FCSTD DOCUMENT  (FreeCAD 1.0R38642 (Git))
Label: heatsink2
License: All rights reserved
LicenseURL: https://en.wikipedia.org/wiki/All_rights_reserved
objects: Sketcher::SketchObject×9, Part::Cut×6, PartDesign::SubShapeBinder×5, Part::Mirroring×5, PartDesign::Fillet×4, PartDesign::Body×4, PartDesign::Pad×3, PartDesign::Plane×3, Fem::FeaturePython×3, PartDesign::AdditivePipe×2, Spreadsheet::Sheet×1, PartDesign::LinearPattern×1, Part::FeaturePython×1, Fem::FemMeshShapeBaseObjectPython×1
note: 71 computed .brp shape members not serialized (recipe doc carries the construction recipe); baked Part::Feature solids carry a one-line shape summary decoded from their .brp

FEATURE [Spreadsheet::Sheet] Spreadsheet
  cells = A1='Base Plate; A2='size; B2(base_size)==50 mm; A3='thickness; B3(base_thickness)==4 mm; A4='radius; B4(base_radius)==3 mm; A5='fillet; B5(base_fillet)==1 mm; A7='Pipes; A8='diameter; B8(pipe_diam)==7 mm; A9='distance; B9(pipe_distance)==(base_size - 3 * pipe_diam) / 4; A10='lower height; B10(pipe_lheight)==30 mm; A11='upper distance; B11(pipe_udistance)==(body_size - 3 * pipe_diam) / 4; A12='lower straight; B12(pipe_lstraight)==5 mm; A13='spline param; B13(pipe_splinep)==20 mm; A14='upper height; B14(pipe_uheight)==5 mm; A15='fillet; B15(pipe_fillet)==2.5 mm; A17='Main body; A18='size; B18(body_size)==100 mm; A19='height; B19(body_height)==75 mm; A21='Fins; A22='fillet; B22(fin_fillet)==2 mm; A23='middle space; B23(fin_mspace)==15 mm; A24='dent; B24(fin_dent)==6 mm; A25='thickness; B25(fin_thickness)==1 mm; A26='count; B26(fin_count)=20
FEATURE [Sketcher::SketchObject] Sketch
  ArcFitTolerance = 1e-06
  AttachmentSupport = -> [XY_Plane]
  FullyConstrained = true
  MakeInternals = false
  MapMode = 5
  expr: Constraints[8] = Spreadsheet.base_size
  sketch-geometry (4):
    g0: LineSegment StartX=-25 StartY=25 StartZ=0 EndX=-25 EndY=-25 EndZ=0
    g1: LineSegment StartX=-25 StartY=-25 StartZ=0 EndX=25 EndY=-25 EndZ=0
    g2: LineSegment StartX=25 StartY=-25 StartZ=0 EndX=25 EndY=25 EndZ=0
    g3: LineSegment StartX=25 StartY=25 StartZ=0 EndX=-25 EndY=25 EndZ=0
  constraints (11):
    c: Coincident(g0,g1)
    c: Coincident(g1,g2)
    c: Coincident(g2,g3)
    c: Coincident(g3,g0)
    c: Vertical(g0)
    c: Vertical(g2)
    c: Horizontal(g1)
    c: Horizontal(g3)
    c: DistanceY(g0,g0) = 50
    c: Equal(g0,g3)
    c: Symmetric(g0,g1,g-1)
FEATURE [PartDesign::Pad] Pad
  Direction = (0,0,1)
  Length = 4
  Length2 = 10
  Profile = -> Sketch
  ReferenceAxis = -> Sketch [N_Axis]
  Refine = true
  Reversed = true
  Suppressed = false
  Type = 0
  expr: Length = Spreadsheet.base_thickness
FEATURE [PartDesign::Fillet] Fillet
  Base = -> Pad [Edge5,Edge8,Edge1,Edge2]
  BaseFeature = -> Pad
  Radius = 3
  Refine = true
  SupportTransform = false
  Suppressed = false
  UseAllEdges = false
  expr: Radius = Spreadsheet.base_radius
FEATURE [Sketcher::SketchObject] Sketch001  label="PipeCenters"
  ArcFitTolerance = 1e-06
  AttachmentSupport = -> [XY_Plane001]
  FullyConstrained = true
  MakeInternals = false
  MapMode = 5
  expr: Constraints[11] = Spreadsheet.pipe_distance + Spreadsheet.pipe_diam / 2
  expr: Constraints[12] = Spreadsheet.pipe_distance + Spreadsheet.pipe_diam / 2
  expr: Constraints[14] = Spreadsheet.pipe_distance + Spreadsheet.pipe_diam
  expr: Constraints[16] = Spreadsheet.pipe_distance + Spreadsheet.pipe_diam
  expr: Constraints[9] = Spreadsheet.base_size
  sketch-geometry (7):
    g0: LineSegment [constr] StartX=-25 StartY=25 StartZ=0 EndX=-25 EndY=-25 EndZ=0
    g1: LineSegment [constr] StartX=-25 StartY=-25 StartZ=0 EndX=25 EndY=-25 EndZ=0
    g2: LineSegment [constr] StartX=25 StartY=-25 StartZ=0 EndX=25 EndY=25 EndZ=0
    g3: LineSegment [constr] StartX=25 StartY=25 StartZ=0 EndX=-25 EndY=25 EndZ=0
    g4: GeomPoint X=-14.25 Y=-14.25 Z=0
    g5: GeomPoint X=-14.25 Y=-1e-15 Z=0
    g6: GeomPoint X=-14.25 Y=14.25 Z=0
  constraints (17):
    c: Coincident(g0,g1)
    c: Coincident(g1,g2)
    c: Coincident(g2,g3)
    c: Coincident(g3,g0)
    c: Vertical(g0)
    c: Vertical(g2)
    c: Horizontal(g1)
    c: Horizontal(g3)
    c: Symmetric(g0,g1,g-1)
    c: DistanceY(g0,g0) = 50
    c: Equal(g2,g3)
    c: DistanceX(g0,g4) = 10.75
    c: DistanceY(g0,g4) = 10.75
    c: Vertical(g5,g4)
    c: DistanceY(g4,g5) = 14.25
    c: Vertical(g5,g6)
    c: DistanceY(g5,g6) = 14.25
FEATURE [PartDesign::SubShapeBinder] Binder  label="LowerEnd"
  BindCopyOnChange = 0
  BindMode = 0
  ClaimChildren = false
  Context = -> Body001 [Binder.]
  Fuse = false
  MakeFace = true
  OffsetFill = false
  OffsetIntersection = false
  OffsetJoinType = 0
  OffsetOpenResult = false
  PartialLoad = false
  Refine = true
  Relative = true
  Support = -> [Sketch001[Vertex1]]
  _Version = 2
FEATURE [Sketcher::SketchObject] Sketch002  label="BaseShape"
  ArcFitTolerance = 1e-06
  AttachmentSupport = -> [XY_Plane001]
  ExternalGeometry = -> [Binder]
  FullyConstrained = true
  MakeInternals = false
  MapMode = 5
  expr: Constraints[1] = Spreadsheet.pipe_diam
  sketch-geometry (1):
    g0: Circle CenterX=-14.25 CenterY=-14.25 CenterZ=0 NormalX=0 NormalY=0 NormalZ=1 AngleXU=0 Radius=3.5
  constraints (2):
    c: Coincident(g0,g-3)
    c: Diameter(g0) = 7
FEATURE [PartDesign::SubShapeBinder] Binder001  label="LowerEnd001"
  BindCopyOnChange = 0
  BindMode = 0
  ClaimChildren = false
  Context = -> Body002 [Binder001.]
  Fuse = false
  MakeFace = true
  OffsetFill = false
  OffsetIntersection = false
  OffsetJoinType = 0
  OffsetOpenResult = false
  PartialLoad = false
  Refine = true
  Relative = true
  Support = -> [Sketch001[Vertex2]]
  _Version = 2
FEATURE [Sketcher::SketchObject] Sketch003  label="BaseShape001"
  ArcFitTolerance = 1e-06
  AttachmentSupport = -> [XY_Plane002]
  ExternalGeometry = -> [Binder001]
  FullyConstrained = true
  MakeInternals = false
  MapMode = 5
  expr: Constraints[1] = Spreadsheet.pipe_diam
  sketch-geometry (1):
    g0: Circle CenterX=-14.25 CenterY=0 CenterZ=0 NormalX=0 NormalY=0 NormalZ=1 AngleXU=0 Radius=3.5
  constraints (2):
    c: Coincident(g0,g-3)
    c: Diameter(g0) = 7
FEATURE [PartDesign::Plane] DatumPlane
  AttachmentOffset = pos=(0,0,30) rot=(0,0,1;0rad)
  AttachmentSupport = -> [XY_Plane]
  Length = 60
  MapMode = 5
  Placement = pos=(0,0,30) rot=(0,0,1;0rad)
  ResizeMode = 0
  Width = 60
  expr: .AttachmentOffset.Base.z = Spreadsheet.pipe_lheight
FEATURE [Sketcher::SketchObject] Sketch006  label="PipeCentersTop"
  ArcFitTolerance = 1e-06
  AttachmentSupport = -> [DatumPlane]
  FullyConstrained = true
  MakeInternals = false
  MapMode = 5
  Placement = pos=(0,0,30) rot=(0,0,1;0rad)
  expr: Constraints[13] = Spreadsheet.pipe_udistance + Spreadsheet.pipe_diam / 2
  expr: Constraints[14] = Spreadsheet.pipe_udistance / 1.5 + Spreadsheet.pipe_diam / 2
  expr: Constraints[15] = Spreadsheet.pipe_udistance + Spreadsheet.pipe_diam
  expr: Constraints[16] = Spreadsheet.pipe_udistance + Spreadsheet.pipe_diam
  expr: Constraints[8] = Spreadsheet.body_size
  sketch-geometry (7):
    g0: LineSegment StartX=-50 StartY=50 StartZ=0 EndX=-50 EndY=-50 EndZ=0
    g1: LineSegment StartX=-50 StartY=-50 StartZ=0 EndX=50 EndY=-50 EndZ=0
    g2: LineSegment StartX=50 StartY=-50 StartZ=0 EndX=50 EndY=50 EndZ=0
    g3: LineSegment StartX=50 StartY=50 StartZ=0 EndX=-50 EndY=50 EndZ=0
    g4: GeomPoint X=-33.3333 Y=-26.75 Z=0
    g5: GeomPoint X=-33.3333 Y=-5e-16 Z=0
    g6: GeomPoint X=-33.3333 Y=26.75 Z=0
  constraints (17):
    c: Coincident(g0,g1)
    c: Coincident(g1,g2)
    c: Coincident(g2,g3)
    c: Coincident(g3,g0)
    c: Vertical(g0)
    c: Vertical(g2)
    c: Horizontal(g1)
    c: Horizontal(g3)
    c: DistanceX(g3,g3) = 100
    c: Equal(g0,g3)
    c: Symmetric(g0,g1,g-1)
    c: Vertical(g6,g5)
    c: Vertical(g5,g4)
    c: DistanceY(g0,g4) = 23.25
    c: DistanceX(g0,g4) = 16.6667
    c: DistanceY(g4,g5) = 26.75
    c: DistanceY(g5,g6) = 26.75
FEATURE [PartDesign::SubShapeBinder] Binder003  label="UpperEnd"
  BindCopyOnChange = 0
  BindMode = 0
  ClaimChildren = false
  Context = -> Body001 [Binder003.]
  Fuse = false
  MakeFace = true
  OffsetFill = false
  OffsetIntersection = false
  OffsetJoinType = 0
  OffsetOpenResult = false
  PartialLoad = false
  Refine = true
  Relative = true
  Support = -> [Body[Sketch006.Vertex5]]
  _Version = 2
FEATURE [PartDesign::Plane] DatumPlane001
  AttachmentSupport = -> [Binder,Z_Axis001,Binder003]
  Length = 103.037
  MapMode = 52
  Placement = pos=(-14.25,-14.25,0) rot=(-0.206426,0.691877,0.691877;3.54873rad)
  ResizeMode = 0
  Width = 156.042
FEATURE [Sketcher::SketchObject] Sketch007  label="Path"
  ArcFitTolerance = 1e-06
  AttachmentSupport = -> [DatumPlane001]
  ExternalGeometry = -> [Binder003]
  FullyConstrained = true
  MakeInternals = false
  MapMode = 5
  Placement = pos=(-14.25,-14.25,0) rot=(-0.206426,0.691877,0.691877;3.54873rad)
  expr: Constraints[19] = Spreadsheet.pipe_splinep
  expr: Constraints[20] = Spreadsheet.pipe_splinep
  expr: Constraints[23] = Spreadsheet.body_height + Spreadsheet.pipe_uheight
  expr: Constraints[4] = Spreadsheet.pipe_lstraight
  sketch-geometry (10):
    g0: LineSegment StartX=0 StartY=0 StartZ=0 EndX=0 EndY=5 EndZ=0
    g1: LineSegment StartX=22.8128 StartY=30 StartZ=0 EndX=22.8128 EndY=35 EndZ=0
    g2-g5: Circle [constr] x4 (B-spline internal-alignment scaffolding for g6; pole/knot coordinates omitted)
    g6: BSplineCurve PolesCount=4 KnotsCount=2 Degree=3 IsPeriodic=0
    g7: GeomPoint [constr] X=0 Y=5 Z=0
    g8: GeomPoint [constr] X=22.8128 Y=35 Z=0
    g9: LineSegment StartX=22.8128 StartY=30 StartZ=0 EndX=22.8128 EndY=110 EndZ=0
  constraints (22):
    c: Coincident(g0,g-1)
    c: PointOnObject(g0,g-2)
    c: Coincident(g1,g-3)
    c: Vertical(g1)
    c: DistanceY(g0,g0) = 5
    c: Weight(g2) = 1
    c: Equal(g2,g3)
    c: Equal(g2,g4)
    c: Equal(g2,g5)
    c: InternalAlignment(g2-g5 -> g6) x4
    c: InternalAlignment(g7,g6)
    c: InternalAlignment(g8,g6)
    c: Coincident(g2,g0)
    c: Coincident(g5,g1)
    c: PointOnObject(g3,g-2)
    c: Vertical(g4,g6)
    c: DistanceY(g4,g6) = 20
    c: DistanceY(g6,g3) = 20
    c: Coincident(g9,g1)
    c: Vertical(g9)
    c: DistanceY(g9,g9) = 80
    c: Equal(g1,g0)
FEATURE [PartDesign::AdditivePipe] AdditivePipe
  AuxilleryCurvelinear = true
  AuxillerySpineTangent = false
  Binormal = (0,0,0)
  Mode = 0
  Profile = -> Sketch002
  Refine = true
  Spine = -> Sketch007
  SpineTangent = false
  Suppressed = false
  Transformation = 0
  Transition = 0
FEATURE [PartDesign::SubShapeBinder] Binder004  label="UpperEnd001"
  BindCopyOnChange = 0
  BindMode = 0
  ClaimChildren = false
  Context = -> Body002 [Binder004.]
  Fuse = false
  MakeFace = true
  OffsetFill = false
  OffsetIntersection = false
  OffsetJoinType = 0
  OffsetOpenResult = false
  PartialLoad = false
  Refine = true
  Relative = true
  Support = -> [Body[Sketch006.Vertex6]]
  _Version = 2
FEATURE [PartDesign::Plane] DatumPlane002
  AttachmentSupport = -> [Binder001,Z_Axis002,Binder004]
  Length = 80.1063
  MapMode = 52
  Placement = pos=(-14.25,-1e-15,0) rot=(0,0.707107,0.707107;3.14159rad)
  ResizeMode = 0
  Width = 153.273
FEATURE [Sketcher::SketchObject] Sketch008  label="Path001"
  ArcFitTolerance = 1e-06
  AttachmentSupport = -> [DatumPlane002]
  ExternalGeometry = -> [Binder004]
  FullyConstrained = true
  MakeInternals = false
  MapMode = 5
  Placement = pos=(-14.25,-1e-15,0) rot=(0,0.707107,0.707107;3.14159rad)
  expr: Constraints[20] = Spreadsheet.pipe_splinep
  expr: Constraints[21] = Spreadsheet.pipe_splinep
  expr: Constraints[24] = Spreadsheet.body_height + Spreadsheet.pipe_uheight
  expr: Constraints[4] = Spreadsheet.pipe_lstraight
  sketch-geometry (10):
    g0: LineSegment StartX=0 StartY=0 StartZ=0 EndX=0 EndY=5 EndZ=0
    g1: LineSegment StartX=19.0833 StartY=30 StartZ=0 EndX=19.0833 EndY=35 EndZ=0
    g2-g5: Circle [constr] x4 (B-spline internal-alignment scaffolding for g6; pole/knot coordinates omitted)
    g6: BSplineCurve PolesCount=4 KnotsCount=2 Degree=3 IsPeriodic=0
    g7: GeomPoint [constr] X=0 Y=5 Z=0
    g8: GeomPoint [constr] X=19.0833 Y=35 Z=0
    g9: LineSegment StartX=19.0833 StartY=30 StartZ=0 EndX=19.0833 EndY=110 EndZ=0
  constraints (22):
    c: Coincident(g0,g-1)
    c: Vertical(g0)
    c: Coincident(g1,g-3)
    c: Vertical(g1)
    c: DistanceY(g0,g0) = 5
    c: Equal(g1,g0)
    c: Weight(g2) = 1
    c: Equal(g2,g3)
    c: Equal(g2,g4)
    c: Equal(g2,g5)
    c: InternalAlignment(g2-g5 -> g6) x4
    c: InternalAlignment(g7,g6)
    c: InternalAlignment(g8,g6)
    c: Coincident(g2,g0)
    c: Coincident(g5,g1)
    c: Vertical(g4,g6)
    c: PointOnObject(g3,g-2)
    c: DistanceY(g6,g3) = 20
    c: DistanceY(g4,g6) = 20
    c: Coincident(g9,g1)
    c: Vertical(g9)
    c: DistanceY(g9,g9) = 80
FEATURE [PartDesign::AdditivePipe] AdditivePipe001
  AuxilleryCurvelinear = true
  AuxillerySpineTangent = false
  Binormal = (0,0,0)
  Mode = 0
  Profile = -> Sketch003
  Refine = true
  Spine = -> Sketch008
  SpineTangent = false
  Suppressed = false
  Transformation = 0
  Transition = 0
FEATURE [PartDesign::Fillet] Fillet001
  Base = -> AdditivePipe [Edge7]
  BaseFeature = -> AdditivePipe
  Radius = 2.5
  Refine = true
  SupportTransform = false
  Suppressed = false
  UseAllEdges = false
  expr: Radius = Spreadsheet.pipe_fillet
FEATURE [PartDesign::Body] Body001  label="CornerPipe"
  AllowCompound = false
  Group = -> [Binder,Sketch002,Binder003,DatumPlane001,Sketch007,AdditivePipe,Fillet001]
  Origin = -> Origin001
  Tip = -> Fillet001
FEATURE [Part::Mirroring] Part__Mirroring  label="CornerPipe (Mirror #1)"
  Base = (0,0,0)
  Normal = (0,1,0)
  Source = -> Body001
FEATURE [Part::Mirroring] Part__Mirroring001  label="CornerPipe (Mirror #2)"
  Base = (0,0,0)
  Normal = (1,0,0)
  Source = -> Body001
FEATURE [Part::Mirroring] Part__Mirroring002  label="CornerPipe (Mirror #3)"
  Base = (0,0,0)
  Normal = (0,1,0)
  Source = -> Part__Mirroring001
FEATURE [PartDesign::Fillet] Fillet002
  Base = -> AdditivePipe001 [Edge7]
  BaseFeature = -> AdditivePipe001
  Radius = 2.5
  Refine = true
  SupportTransform = false
  Suppressed = false
  UseAllEdges = false
  expr: Radius = Spreadsheet.pipe_fillet
FEATURE [PartDesign::Body] Body002  label="MiddlePipe"
  AllowCompound = false
  Group = -> [Binder001,Sketch003,Binder004,DatumPlane002,Sketch008,AdditivePipe001,Fillet002]
  Origin = -> Origin002
  Tip = -> Fillet002
FEATURE [Part::Mirroring] Part__Mirroring003  label="MiddlePipe (Mirror #1)"
  Base = (0,0,0)
  Normal = (1,0,0)
  Source = -> Body002
FEATURE [PartDesign::Fillet] Fillet003
  Base = -> Pad [Edge6,Edge3,Edge11,Edge9,Edge5,Edge2,Edge8,Edge1]
  BaseFeature = -> Pad
  Radius = 1
  Refine = true
  SupportTransform = false
  Suppressed = false
  UseAllEdges = false
  expr: Radius = Spreadsheet.base_fillet
FEATURE [PartDesign::Body] Body  label="Base"
  AllowCompound = false
  Group = -> [Sketch,Pad,Fillet,DatumPlane,Sketch006,Fillet003]
  Origin = -> Origin
  Tip = -> Fillet003
FEATURE [Sketcher::SketchObject] Sketch009
  ArcFitTolerance = 1e-06
  AttachmentSupport = -> [XY_Plane003]
  FullyConstrained = true
  MakeInternals = false
  MapMode = 5
  expr: Constraints[10] = Spreadsheet.body_size
  expr: Constraints[59] = Spreadsheet.fin_fillet
  expr: Constraints[61] = Spreadsheet.fin_mspace / 2
  expr: Constraints[62] = Spreadsheet.fin_dent
  expr: Constraints[63] = Spreadsheet.fin_dent
  sketch-geometry (28):
    g0: LineSegment [constr] StartX=-50 StartY=50 StartZ=0 EndX=-50 EndY=-50 EndZ=0
    g1: LineSegment [constr] StartX=-50 StartY=-50 StartZ=0 EndX=50 EndY=-50 EndZ=0
    g2: LineSegment [constr] StartX=50 StartY=-50 StartZ=0 EndX=50 EndY=50 EndZ=0
    g3: LineSegment [constr] StartX=50 StartY=50 StartZ=0 EndX=-50 EndY=50 EndZ=0
    g4: LineSegment StartX=-9.5 StartY=50 StartZ=0 EndX=-48 EndY=50 EndZ=0
    g5: LineSegment StartX=-50 StartY=48 StartZ=0 EndX=-50 EndY=46 EndZ=0
    g6: LineSegment StartX=-48 StartY=44 StartZ=0 EndX=-46 EndY=44 EndZ=0
    g7: LineSegment StartX=-44 StartY=42 StartZ=0 EndX=-44 EndY=-42 EndZ=0
    g8: LineSegment StartX=-46 StartY=-44 StartZ=0 EndX=-48 EndY=-44 EndZ=0
    g9: LineSegment StartX=-50 StartY=-46 StartZ=0 EndX=-50 EndY=-48 EndZ=0
    g10: LineSegment StartX=-48 StartY=-50 StartZ=0 EndX=-9.5 EndY=-50 EndZ=0
    g11: LineSegment StartX=-7.5 StartY=-48 StartZ=0 EndX=-7.5 EndY=48 EndZ=0
    g12: ArcOfCircle CenterX=-48 CenterY=-48 CenterZ=0 NormalX=0 NormalY=0 NormalZ=1 AngleXU=0 Radius=2 StartAngle=3.14159 EndAngle=4.71239
    g13: GeomPoint [constr] X=-50 Y=-50 Z=0
    g14: ArcOfCircle CenterX=-48 CenterY=-46 CenterZ=0 NormalX=0 NormalY=0 NormalZ=1 AngleXU=0 Radius=2 StartAngle=1.5708 EndAngle=3.14159
    g15: GeomPoint [constr] X=-50 Y=-44 Z=0
    g16: ArcOfCircle CenterX=-46 CenterY=-42 CenterZ=0 NormalX=0 NormalY=0 NormalZ=1 AngleXU=0 Radius=2 StartAngle=4.71239 EndAngle=6.28319
    g17: GeomPoint [constr] X=-44 Y=-44 Z=0
    g18: ArcOfCircle CenterX=-46 CenterY=42 CenterZ=0 NormalX=0 NormalY=0 NormalZ=1 AngleXU=0 Radius=2 StartAngle=-9e-16 EndAngle=1.5708
    g19: GeomPoint [constr] X=-44 Y=44 Z=0
    g20: ArcOfCircle CenterX=-48 CenterY=46 CenterZ=0 NormalX=0 NormalY=0 NormalZ=1 AngleXU=0 Radius=2 StartAngle=3.14159 EndAngle=4.71239
    g21: GeomPoint [constr] X=-50 Y=44 Z=0
    g22: ArcOfCircle CenterX=-48 CenterY=48 CenterZ=0 NormalX=0 NormalY=0 NormalZ=1 AngleXU=0 Radius=2 StartAngle=1.5708 EndAngle=3.14159
    g23: GeomPoint [constr] X=-50 Y=50 Z=0
    g24: ArcOfCircle CenterX=-9.5 CenterY=48 CenterZ=0 NormalX=0 NormalY=0 NormalZ=1 AngleXU=0 Radius=2 StartAngle=-3.6e-15 EndAngle=1.5708
    g25: GeomPoint [constr] X=-7.5 Y=50 Z=0
    g26: ArcOfCircle CenterX=-9.5 CenterY=-48 CenterZ=0 NormalX=0 NormalY=0 NormalZ=1 AngleXU=0 Radius=2 StartAngle=4.71239 EndAngle=6.28319
    g27: GeomPoint [constr] X=-7.5 Y=-50 Z=0
  constraints (64):
    c: Coincident(g0,g1)
    c: Coincident(g1,g2)
    c: Coincident(g2,g3)
    c: Coincident(g3,g0)
    c: Vertical(g0)
    c: Vertical(g2)
    c: Horizontal(g1)
    c: Horizontal(g3)
    c: Equal(g0,g3)
    c: Symmetric(g0,g1,g-1)
    c: DistanceX(g1,g1) = 100
    c: PointOnObject(g25,g3)
    c: Coincident(g23,g0)
    c: PointOnObject(g21,g0)
    c: Horizontal(g6)
    c: Vertical(g7)
    c: PointOnObject(g15,g0)
    c: Horizontal(g8)
    c: Coincident(g13,g0)
    c: PointOnObject(g27,g1)
    c: Vertical(g11)
    c: PointOnObject(g13,g10)
    c: PointOnObject(g13,g9)
    c: Tangent(g10,g12) = -1.5708
    c: Tangent(g9,g12) = -1.5708
    c: PointOnObject(g15,g9)
    c: PointOnObject(g15,g8)
    c: Tangent(g9,g14) = -1.5708
    c: Tangent(g8,g14) = -1.5708
    c: PointOnObject(g17,g8)
    c: PointOnObject(g17,g7)
    c: Tangent(g8,g16) = 1.5708
    c: Tangent(g7,g16) = 1.5708
    c: PointOnObject(g19,g6)
    c: Tangent(g7,g18) = 1.5708
    c: Tangent(g6,g18) = 1.5708
    c: PointOnObject(g21,g6)
    c: PointOnObject(g21,g5)
    c: Tangent(g6,g20) = -1.5708
    c: Tangent(g5,g20) = -1.5708
    c: PointOnObject(g23,g5)
    c: PointOnObject(g23,g4)
    c: Tangent(g5,g22) = -1.5708
    c: Tangent(g4,g22) = -1.5708
    c: PointOnObject(g25,g4)
    c: PointOnObject(g25,g11)
    c: Tangent(g4,g24) = -1.5708
    c: Tangent(g11,g24) = -1.5708
    c: PointOnObject(g27,g11)
    c: PointOnObject(g27,g10)
    c: Tangent(g11,g26) = -1.5708
    c: Tangent(g10,g26) = -1.5708
    c: Equal(g24,g22)
    c: Equal(g22,g20)
    c: Equal(g20,g18)
    c: Equal(g18,g26)
    c: Equal(g26,g12)
    c: Equal(g12,g14)
    c: Equal(g14,g16)
    c: Radius(g26) = 2
    c: Symmetric(g17,g19,g-1)
    c: DistanceX(g11,g-1) = 7.5
    c: DistanceX(g0,g17) = 6
    c: DistanceY(g0,g15) = 6
FEATURE [PartDesign::SubShapeBinder] Binder005
  BindCopyOnChange = 0
  BindMode = 0
  ClaimChildren = false
  Context = -> Body003 [Binder005.]
  Fuse = false
  MakeFace = true
  OffsetFill = false
  OffsetIntersection = false
  OffsetJoinType = 0
  OffsetOpenResult = false
  PartialLoad = false
  Refine = true
  Relative = true
  Support = -> [Body[Sketch006.Vertex6]]
  _Version = 2
FEATURE [Sketcher::SketchObject] Sketch010
  ArcFitTolerance = 1e-06
  AttachmentSupport = -> [XY_Plane003]
  ExternalGeometry = -> [Binder005]
  FullyConstrained = true
  MakeInternals = false
  MapMode = 5
  expr: Constraints[1] = Spreadsheet.pipe_diam / 2
  sketch-geometry (1):
    g0: Circle CenterX=-33.3333 CenterY=0 CenterZ=0 NormalX=0 NormalY=0 NormalZ=1 AngleXU=0 Radius=1.75
  constraints (2):
    c: Coincident(g0,g-3)
    c: Diameter(g0) = 3.5
FEATURE [PartDesign::Pad] Pad002
  Direction = (0,0,1)
  Length = 75
  Length2 = 10
  Profile = -> Sketch010
  ReferenceAxis = -> Sketch010 [N_Axis]
  Refine = true
  Suppressed = false
  Type = 0
  expr: Length = Spreadsheet.body_height
FEATURE [PartDesign::Pad] Pad001
  BaseFeature = -> Pad002
  Direction = (0,0,1)
  Length = 1
  Length2 = 10
  Profile = -> Sketch009
  ReferenceAxis = -> Sketch009 [N_Axis]
  Refine = true
  Suppressed = false
  Type = 0
  expr: Length = Spreadsheet.fin_thickness
FEATURE [PartDesign::LinearPattern] LinearPattern
  BaseFeature = -> Pad001
  Direction = -> Sketch009 [N_Axis]
  Length = 75
  Mode = 0
  Occurrences = 20
  Offset = 3.94737
  Originals = -> [Pad001]
  Refine = true
  Suppressed = false
  TransformMode = 0
  expr: Length = Spreadsheet.body_height
  expr: Occurrences = Spreadsheet.fin_count
FEATURE [PartDesign::Body] Body003  label="Fins"
  AllowCompound = false
  Group = -> [Sketch009,Binder005,Sketch010,Pad002,Pad001,LinearPattern]
  Origin = -> Origin003
  Placement = pos=(0,0,30) rot=(0,0,1;0rad)
  Tip = -> LinearPattern
  expr: .Placement.Base.z = Spreadsheet.pipe_lheight
FEATURE [Part::Mirroring] Part__Mirroring004  label="Fins (Mirror #5)"
  Base = (0,0,0)
  Normal = (1,0,0)
  Source = -> Body003
FEATURE [Part::Cut] Cut
  Base = -> Body003
  Refine = true
  Tool = -> Body001
FEATURE [Part::Cut] Cut001
  Base = -> Cut
  Refine = true
  Tool = -> Part__Mirroring
FEATURE [Part::Cut] Cut002  label="CutFins"
  Base = -> Cut001
  Refine = true
  Tool = -> Body002
FEATURE [Part::Cut] Cut003
  Base = -> Part__Mirroring004
  Refine = true
  Tool = -> Part__Mirroring002
FEATURE [Part::Cut] Cut004
  Base = -> Cut003
  Refine = true
  Tool = -> Part__Mirroring001
FEATURE [Part::Cut] Cut005  label="CutFins Mirror"
  Base = -> Cut004
  Refine = true
  Tool = -> Part__Mirroring003
FEATURE [Part::FeaturePython] BooleanFragments  # WARN: FeaturePython — macro-defined, semantics opaque (R4)
  Mode = 0
  Objects = -> [Cut002,Cut005,Body001,Part__Mirroring001,Part__Mirroring002,Part__Mirroring003,Part__Mirroring,Body002,Body]
  Tolerance = 0
FEATURE [Fem::FeaturePython] MeshGroup  label="BaseBody"  # FEM object (typed FeaturePython)
  References = -> [BooleanFragments]
  UseLabel = true
FEATURE [Fem::FeaturePython] MeshGroup001  label="Pipes"  # FEM object (typed FeaturePython)
  References = -> [BooleanFragments]
  UseLabel = true
FEATURE [Fem::FeaturePython] MeshGroup002  label="Bottom"  # FEM object (typed FeaturePython)
  References = -> [BooleanFragments]
  UseLabel = true
FEATURE [Fem::FemMeshShapeBaseObjectPython] FEMMeshGmsh  # FEM object (typed FeaturePython)
  Algorithm2D = 1
  Algorithm3D = 1
  CharacteristicLengthMax = 1
  CharacteristicLengthMin = 0
  CoherenceMesh = true
  ElementDimension = 3
  ElementOrder = 0
  GeometryTolerance = 1e-06
  GroupsOfNodes = false
  HighOrderOptimize = 0
  MeshGroupList = -> [MeshGroup,MeshGroup001,MeshGroup002]
  MeshSizeFromCurvature = 12
  OptimizeNetgen = false
  OptimizeStd = true
  RecombinationAlgorithm = 0
  Recombine3DAll = false
  RecombineAll = false
  SecondOrderLinear = false
  Shape = -> BooleanFragments
  SubdivisionAlgorithm = 0
